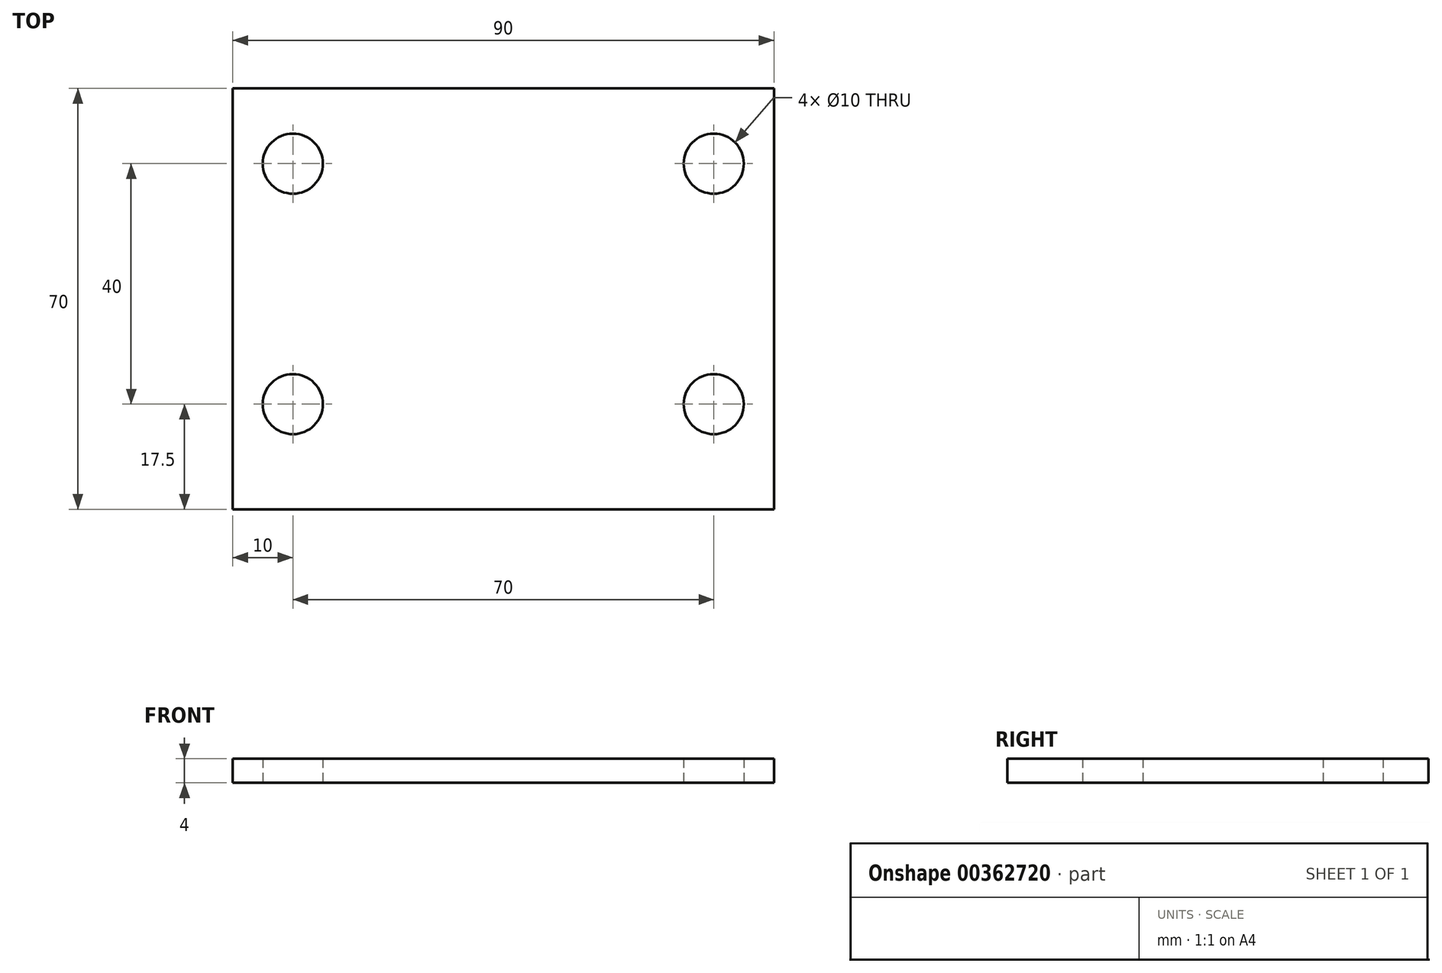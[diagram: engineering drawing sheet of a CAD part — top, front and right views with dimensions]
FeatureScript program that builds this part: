
annotation { "Feature Type Name" : "Feature", "Feature Type Description" : "" }
export const myFeature = defineFeature(function(context is Context, id is Id, definition is map)
    precondition{}
    {
        {
            var Q0;
            Q0=qCreatedBy(makeId("Top.planeOp"),FACE);
            var sketch = newSketch(context, id + "F0", { "sketchPlane" : qUnion([Q0])});
            skLineSegment(sketch, "E0.bottom", {"start": v(-45, 45) * mm, "end": v(45, 45) * mm});
            skLineSegment(sketch, "E0.top", {"start": v(-45, -25) * mm, "end": v(45, -25) * mm});
            skLineSegment(sketch, "E0.left", {"start": v(-45, 45) * mm, "end": v(-45, -25) * mm});
            skLineSegment(sketch, "E0.right", {"start": v(45, 45) * mm, "end": v(45, -25) * mm});
            skLineSegment(sketch, "E1.bottom", {"start": v(-25, 25) * mm, "end": v(25, 25) * mm, "construction": true});
            skLineSegment(sketch, "E1.top", {"start": v(-25, -25) * mm, "end": v(25, -25) * mm, "construction": true});
            skLineSegment(sketch, "E1.left", {"start": v(-25, 25) * mm, "end": v(-25, -25) * mm, "construction": true});
            skLineSegment(sketch, "E1.right", {"start": v(25, 25) * mm, "end": v(25, -25) * mm, "construction": true});
            skCircle(sketch, "E2", {"center": v(-35, 32.5) * mm, "radius": 5 * mm});
            skLineSegment(sketch, "E3", {"start": v(-35, 32.5) * mm, "end": v(49.8, 32.5) * mm, "construction": true});
            skLineSegment(sketch, "E4", {"start": v(-35, 32.64) * mm, "end": v(-35, -43.7) * mm, "construction": true});
            skCircle(sketch, "E5", {"center": v(35, 32.5) * mm, "radius": 5 * mm});
            skCircle(sketch, "E6", {"center": v(35, -7.5) * mm, "radius": 5 * mm});
            skLineSegment(sketch, "E7", {"start": v(35, 32.83) * mm, "end": v(35, -47.11) * mm, "construction": true});
            skLineSegment(sketch, "E8", {"start": v(49.8, -7.5) * mm, "end": v(-35, -7.5) * mm, "construction": true});
            skCircle(sketch, "E9", {"center": v(-35, -7.5) * mm, "radius": 5 * mm});
            skSolve(sketch);
        }
        {
            var Q0;
            Q0=makeQuery(id+"F0.imprint","IMPRINT",FACE,{"disambiguationData":[TD([[makeQuery(id+"F0.imprint","IMPRINT",EDGE,{"derivedFrom":sQuery(id+"F0.wireOp",EDGE,"E0.bottom")}),-1.0]])]});
            extrude(context, id + "F1", {"entities" : qUnion([Q0]), "depth" : 4 * mm});
        }
    });
